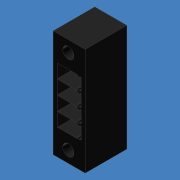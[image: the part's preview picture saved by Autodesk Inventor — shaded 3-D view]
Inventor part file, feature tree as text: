
AUTODESK INVENTOR PART (.ipt)
format: ipt  version: 2011 (Build 150239000, 239)  size: 136,704 bytes
history: native  units: mm (DEFAULTED — no unit token found)
features: sketch x3, extrude x2, hole x1, mirror x1, pattern_linear x1
ambient origin geometry x8: Origin, YZ Plane, XZ Plane, XY Plane, X Axis, Y Axis, Z Axis, Center Point
bodies: Solid1 (feature_tree)
feature tree (8):
  extrude  "Extrusion1"  Depth=24.2316mm
  hole  "Hole1"  [1 undecoded]
  mirror  "Mirror1"
  extrude  "Extrusion2"  Depth=3.048mm
  pattern_linear  "Rectangular Pattern1"  Spacing1=5.334mm  [1 undecoded]
  sketch  "Sketch1"  dims[d0=7.239mm d1=24.2316mm]
  sketch  "Sketch2"  dims[d2=9.398mm d3=0.0mm d4=9.525mm]
  sketch  "Sketch3"  dims[d5=2.54mm d6=12.7mm d7=9.525mm d8=6.35mm d9=14.3117mm d10=6.35mm d11=20.594885mm d12=3.048mm d13=5.334mm d14=4.572mm d16=2.032mm d17=2.794mm d18=0.508mm d19=5.8293mm d20=6.35mm d21=0.0mm d22=3.429mm d23=40.0mm d25=3.175mm]
note: 2 required parameter values undecoded (feature->parameter linkage not recoverable at this tier; creation-order binding heuristic only, values carry confidence <= 0.55)
